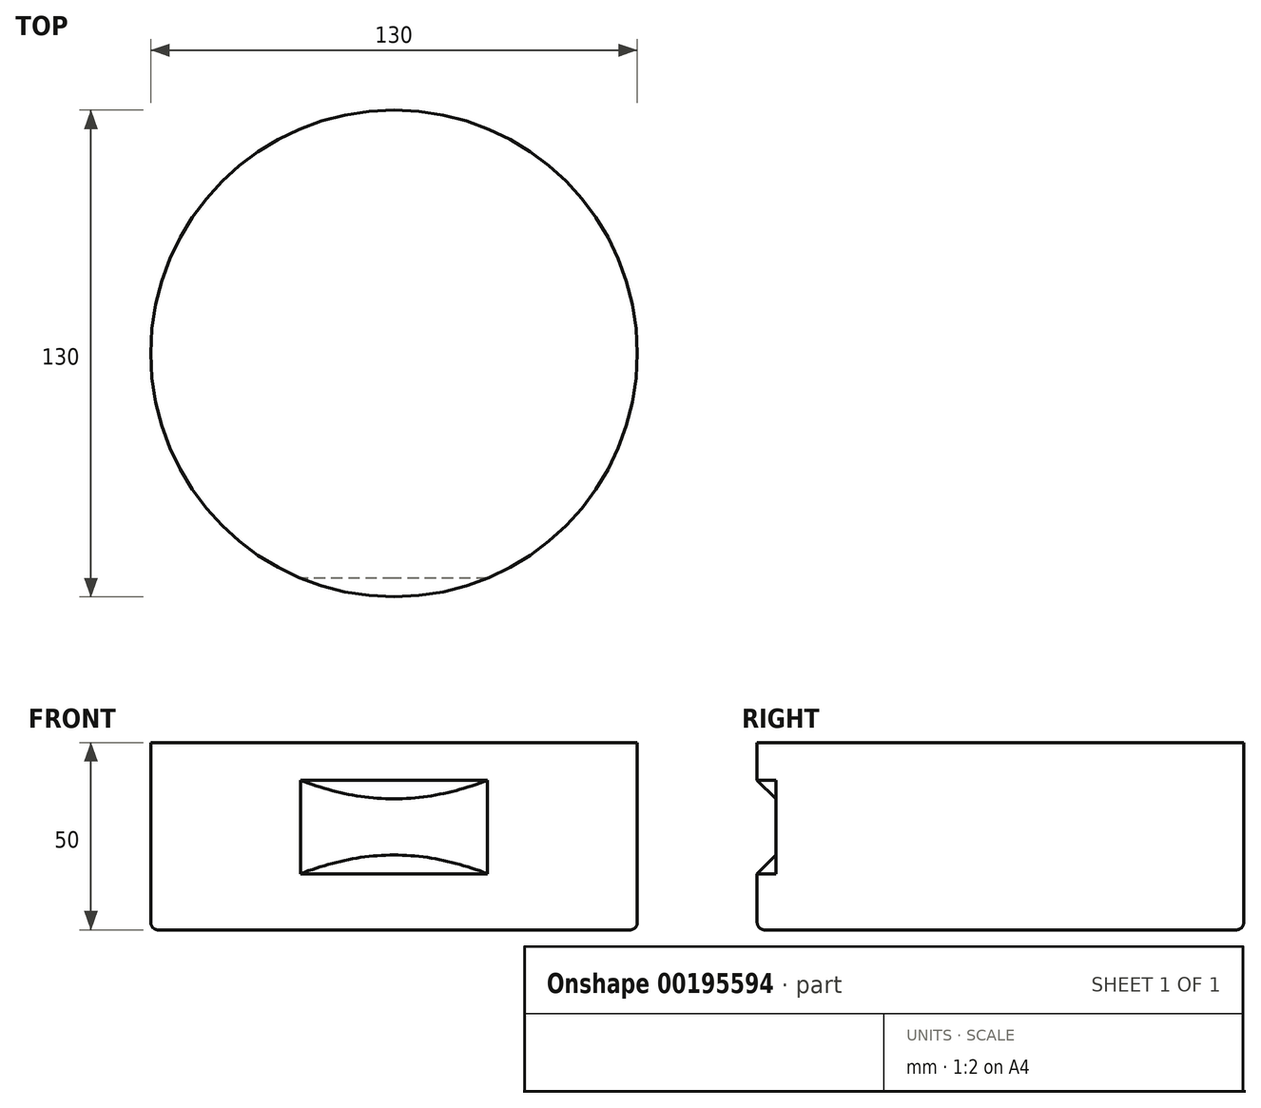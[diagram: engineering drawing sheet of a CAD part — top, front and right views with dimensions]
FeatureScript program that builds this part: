
annotation { "Feature Type Name" : "Feature", "Feature Type Description" : "" }
export const myFeature = defineFeature(function(context is Context, id is Id, definition is map)
    precondition{}
    {
        {
            var Q0;
            Q0=qCreatedBy(makeId("Top.planeOp"),FACE);
            var sketch = newSketch(context, id + "F0", { "sketchPlane" : qUnion([Q0])});
            skCircle(sketch, "E0", {"center": v(0, 0) * mm, "radius": 65 * mm});
            skSolve(sketch);
        }
        {
            var Q0;
            Q0 = qSketchRegion(id + "F0", true);
            extrude(context, id + "F1", {"entities" : qUnion([Q0]), "depth" : 50 * mm});
        }
        {
            var Q0;
            Q0=makeQuery(id+"F1.opExtrude","CAP_EDGE",EDGE,{"disambiguationData":[OSD([sQuery(id+"F0.wireOp",EDGE,"E0")])],"isStart":true});
            fillet(context, id + "F2", {"entities" : qUnion([Q0]), "radius" : 2 * mm, "tangentPropagation" : true, "allowEdgeOverflow" : false});
        }
        {
            var Q0;
            Q0=qCreatedBy(makeId("Front.planeOp"),FACE);
            cPlane(context, id + "F3", {"entities" : qUnion([Q0]), "cplaneType" : CPlaneType.OFFSET, "offset" : 60 * mm, "width" : 150 * mm, "height" : 150 * mm});
        }
        {
            var Q0;
            Q0=qCreatedBy(id+"F3.planeOp",FACE);
            var sketch = newSketch(context, id + "F4", { "sketchPlane" : qUnion([Q0])});
            skLineSegment(sketch, "E1.bottom", {"start": v(-25, 35) * mm, "end": v(25, 35) * mm});
            skLineSegment(sketch, "E1.top", {"start": v(-25, 20) * mm, "end": v(25, 20) * mm});
            skLineSegment(sketch, "E1.left", {"start": v(-25, 35) * mm, "end": v(-25, 20) * mm});
            skLineSegment(sketch, "E1.right", {"start": v(25, 35) * mm, "end": v(25, 20) * mm});
            skSolve(sketch);
        }
        {
            var Q0;
            Q0=makeQuery(id+"F4.imprint","IMPRINT",FACE,{"disambiguationData":[TD([[makeQuery(id+"F4.imprint","IMPRINT",EDGE,{"derivedFrom":sQuery(id+"F4.wireOp",EDGE,"E1.bottom")}),-1.0]])]});
            extrude(context, id + "F5", {"entities" : qUnion([Q0]), "operationType" : NewBodyOperationType.REMOVE, "depth" : 25 * mm});
        }
        {
            var Q0;
            Q0=makeQuery(id+"F5.boolean.opBoolean","INTERSECT",EDGE,{"derivedFrom":[makeQuery(id+"F1.opExtrude","SWEPT_FACE",FACE,{"disambiguationData":[OSD([sQuery(id+"F0.wireOp",EDGE,"E0")])]}),makeQuery(id+"F5.opExtrude","SWEPT_FACE",FACE,{"disambiguationData":[OSD([sQuery(id+"F4.wireOp",EDGE,"E1.top")])]})]});
            var Q1;
            Q1=makeQuery(id+"F5.boolean.opBoolean","INTERSECT",EDGE,{"derivedFrom":[makeQuery(id+"F1.opExtrude","SWEPT_FACE",FACE,{"disambiguationData":[OSD([sQuery(id+"F0.wireOp",EDGE,"E0")])]}),makeQuery(id+"F5.opExtrude","SWEPT_FACE",FACE,{"disambiguationData":[OSD([sQuery(id+"F4.wireOp",EDGE,"E1.bottom")])]})]});
            chamfer(context, id + "F6", {"entities" : qUnion([Q0, Q1]), "width" : 5 * mm, "tangentPropagation" : true});
        }
    });
